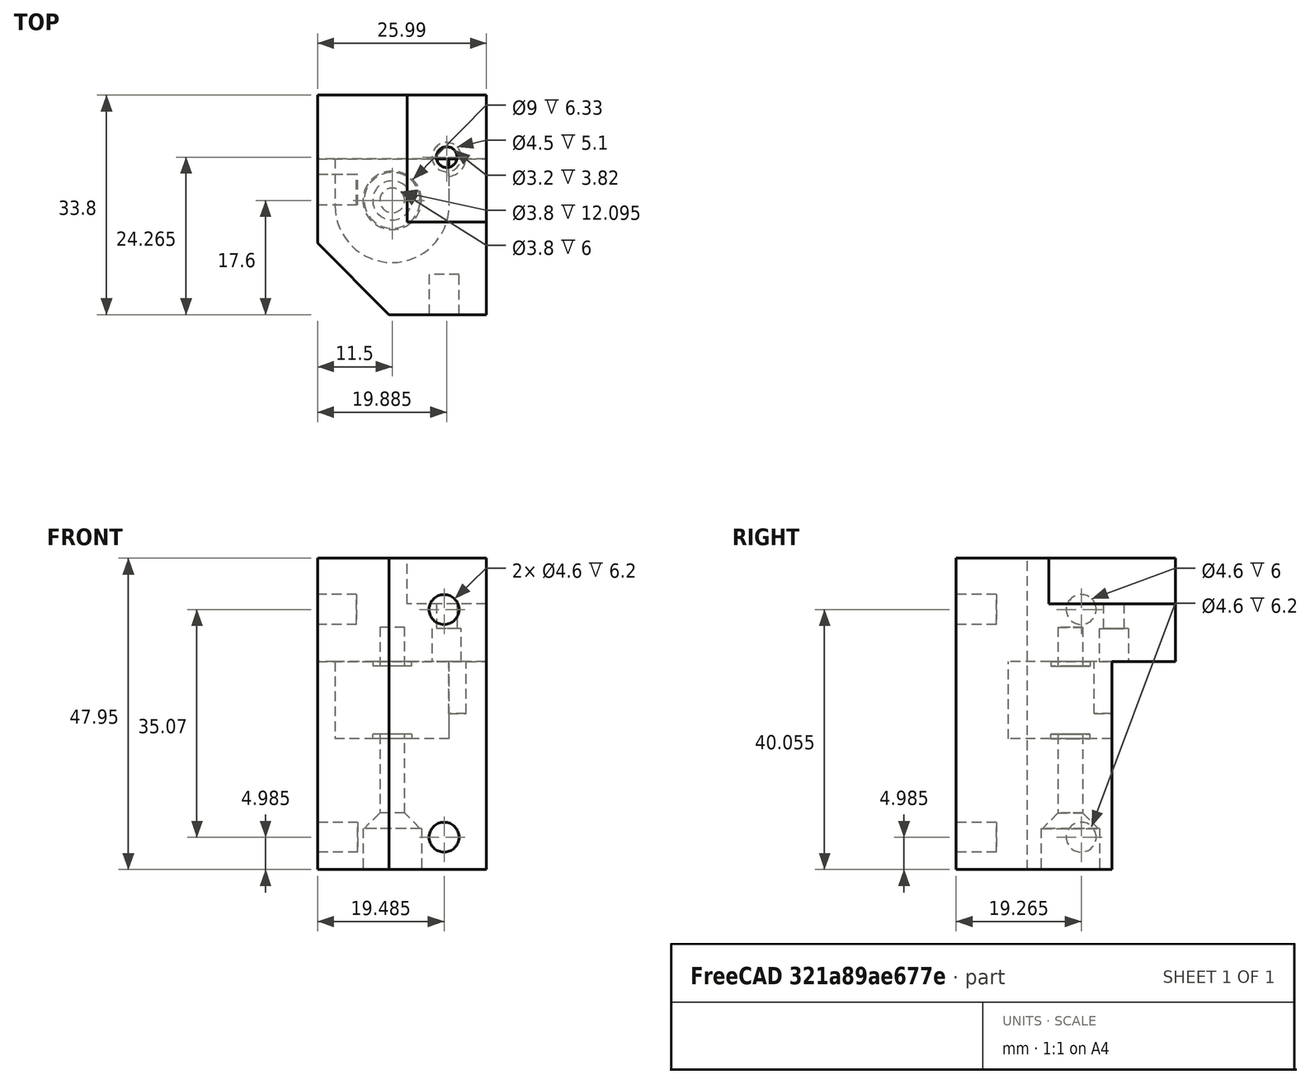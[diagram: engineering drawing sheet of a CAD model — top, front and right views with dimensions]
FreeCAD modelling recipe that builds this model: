
FCSTD DOCUMENT  (FreeCAD 1.0R38641 +468 (Git))
Label: k1_front_idler_left
License: All rights reserved
LicenseURL: https://en.wikipedia.org/wiki/All_rights_reserved
objects: Part::Feature×1, PartDesign::FeatureBase×1, PartDesign::Body×1, App::Link×1, App::Part×1
note: 4 computed .brp shape members not serialized (recipe doc carries the construction recipe); baked Part::Feature solids carry a one-line shape summary decoded from their .brp
EXTERNAL_REF file=cad_powge_pulley.FCStd obj=Part

FEATURE [Part::Feature] Part__Feature  label="step"
  shape: bbox 25.99 x 33.8 x 47.95 mm, 39 faces (baked)
FEATURE [PartDesign::FeatureBase] BaseFeature
  BaseFeature = -> Part__Feature
  Suppressed = false
FEATURE [PartDesign::Body] Body  label="k1_front_idler_left"
  AllowCompound = false
  BaseFeature = -> Part__Feature
  Group = -> [BaseFeature]
  Origin = -> Origin001
  Tip = -> BaseFeature
FEATURE [App::Link] Link  label="cad_powge_pulley"
  LinkPlacement = pos=(11.5,17.6,20.825) rot=(0,0,1;0rad)
  LinkedObject = -> <external cad_powge_pulley.FCStd>#Part
  Placement = pos=(11.5,17.6,20.825) rot=(0,0,1;0rad)
FEATURE [App::Part] Part  label="k1_front_idler_left_part"
  Group = -> [Body,Link]
  Origin = -> Origin

RESOLVED EXTERNAL PARTS (link-assembly join: the EXTERNAL_REF files above that resolve inside this repo's crawl, each included once):
---- part cad_powge_pulley.FCStd = doc fcstd_d49da9a9e340 ----
FCSTD DOCUMENT  (FreeCAD 1.0R38641 +468 (Git))
Label: cad_powge_pulley
License: All rights reserved
LicenseURL: https://en.wikipedia.org/wiki/All_rights_reserved
objects: Sketcher::SketchObject×1, PartDesign::Revolution×1, PartDesign::Body×1, App::Part×1
note: 6 computed .brp shape members not serialized (recipe doc carries the construction recipe); baked Part::Feature solids carry a one-line shape summary decoded from their .brp

FEATURE [Sketcher::SketchObject] Sketch
  ArcFitTolerance = 1e-06
  AttachmentSupport = -> [XZ_Plane]
  FullyConstrained = true
  MakeInternals = false
  MapMode = 5
  Placement = pos=(0,0,0) rot=(1,0,0;1.5708rad)
  sketch-geometry (8):
    g0: LineSegment StartX=6.1 StartY=9.3 StartZ=0 EndX=6.1 EndY=1.2 EndZ=0
    g1: LineSegment StartX=6.1 StartY=1.2 StartZ=0 EndX=8 EndY=1.2 EndZ=0
    g2: LineSegment StartX=8 StartY=1.2 StartZ=0 EndX=8 EndY=0 EndZ=0
    g3: LineSegment StartX=8 StartY=0 StartZ=0 EndX=2 EndY=0 EndZ=0
    g4: LineSegment StartX=2 StartY=0 StartZ=0 EndX=2 EndY=10.5 EndZ=0
    g5: LineSegment StartX=2 StartY=10.5 StartZ=0 EndX=8 EndY=10.5 EndZ=0
    g6: LineSegment StartX=8 StartY=10.5 StartZ=0 EndX=8 EndY=9.3 EndZ=0
    g7: LineSegment StartX=8 StartY=9.3 StartZ=0 EndX=6.1 EndY=9.3 EndZ=0
  constraints (24):
    c: Vertical(g0)
    c: Coincident(g1,g0)
    c: Horizontal(g1)
    c: Coincident(g2,g1)
    c: PointOnObject(g2,g-1)
    c: Vertical(g2)
    c: Coincident(g3,g2)
    c: PointOnObject(g3,g-1)
    c: Coincident(g4,g3)
    c: Vertical(g4)
    c: Coincident(g5,g4)
    c: Horizontal(g5)
    c: Coincident(g6,g5)
    c: Vertical(g6)
    c: Coincident(g7,g6)
    c: Horizontal(g7)
    c: Coincident(g0,g7)
    c: Equal(g5,g3)
    c: Equal(g6,g2)
    c: Distance(g4,g-2) = 2
    c: Distance(g5,g-2) = 8
    c: DistanceY(g0,g0) = 8.1
    c: DistanceY(g4,g4) = 10.5
    c: Distance(g0,g-2) = 6.1
FEATURE [PartDesign::Revolution] Revolution
  Angle = 360
  Angle2 = 60
  Axis = (0,2e-16,1)
  Base = (0,0,0)
  Placement = pos=(0,0,0) rot=(1,0,0;1.5708rad)
  Profile = -> Sketch
  ReferenceAxis = -> Sketch [V_Axis]
  Refine = true
  Reversed = true
  Suppressed = false
  Type = 0
FEATURE [PartDesign::Body] Body  label="powge_pulley"
  AllowCompound = false
  Group = -> [Sketch,Revolution]
  Origin = -> Origin
  Tip = -> Revolution
FEATURE [App::Part] Part  label="powge_pulley_part"
  Group = -> [Body]
  Origin = -> Origin001
